# Revit family: Electrical_Switchgear_Modelec_Collection-Iris-by-Modelec_FRA888
name_source: partatom
category: Installations électriques
units: mm (PartAtom-declared; Revit-internal decimal feet)

## family parameters
Conserver l'orientation des annotations = Non
Cote de connecteur circulaire = Utiliser le diamètre
Couper avec des vides une fois chargée = Non
Hôte = Face
Numéro OmniClass = 23.80.50.11.14
Partagée = Non
Repere pour localisation dans la piece = Non
Titre OmniClass = Switches
Type d'élément = Normal

## types (1)
- Par défaut - veuillez charger le catalogue des types de familles Revit
    Apparent Load = 0 VA
    B1 = Oui
    B2 = Non
    C1 = Non
    Couleur du Mécanisme = Modelec - Plastique - Toucher Doux Blanc
    Description = Une collection héritée des esthétiques des années 1930, la collection Iris de MODELEC est douce : sa forme ronde aux bords doux est associée à la manette «drop», et elle se laisse caresser par l'œil. Depuis 2023, la collection est également disponible en porcelaine noire ou blanche.
    Description du Connecteur = Interrupteur
    Elévation par défaut = 0 mm  [stored 0 ft]
    Fabricant = Modelec
    Installation instructions = https://www.modelec.com
    K1 = Non
    M1 = Non
    Modèle = Iris Collection
    Number of Poles = 1
    Power Factor = 1
    Product Documentation Link = https://www.modelec.com
    Product Page URL = https://www.modelec.com
    Product data url = https://bimobject.com
    Quantité 1 = 3
    Quantité 2 = 3
    R1 = Non
    SC = Non
    U1 = Non
    URL = https://www.modelec.com
    Version = 1
    Voltage = 220 V
    Weight - Mass = 0.05 kg

note: [stored X ft] marks values corroborated as IEEE doubles in the binary element streams (Revit-internal decimal feet)

## geometry (parser evidence)
native form markers: Sweep x3
no freeform markers — native parametric forms only
